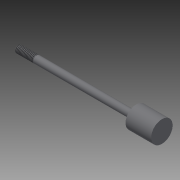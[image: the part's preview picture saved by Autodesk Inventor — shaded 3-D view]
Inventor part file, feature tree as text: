
AUTODESK INVENTOR PART (.ipt)
format: ipt  version: 2014 (Build 180170000, 170)  size: 131,072 bytes
history: native  units: in
note: dims shown in document units (in); Inventor stores cm internally (conversion verified against a paired STEP export)
features: other x49, revolve x3, sketch x3, thread x1
ambient origin geometry x8: Origin, YZ Plane, XZ Plane, XY Plane, X Axis, Y Axis, Z Axis, Center Point
bodies: Solid1 (feature_tree)
feature tree (56):
  revolve  "Revolution1"  [1 undecoded]
  thread  "Thread1"  [1 undecoded]
  revolve  "Revolution2"  [1 undecoded]
  revolve  "Revolution3"  [1 undecoded]
  other  "h1_XY"
  other  "h1_YZ"
  other  "h1_ZX"
  other  "h1_X"
  other  "h1_Y"
  other  "h1_Z"
  other  "h1_Center"
  other  "h2_XY"
  other  "h2_YZ"
  other  "h2_ZX"
  other  "h2_X"
  other  "h2_Y"
  other  "h2_Z"
  other  "h2_Center"
  other  "k1_XY"
  other  "k1_YZ"
  other  "k1_ZX"
  other  "k1_X"
  other  "k1_Y"
  other  "k1_Z"
  other  "k1_Center"
  other  "k2_XY"
  other  "k2_YZ"
  other  "k2_ZX"
  other  "k2_X"
  other  "k2_Y"
  other  "k2_Z"
  other  "k2_Center"
  other  "start_XY"
  other  "start_YZ"
  other  "start_ZX"
  other  "start_X"
  other  "start_Y"
  other  "start_Z"
  other  "start_Center"
  other  "to_prc_XY"
  other  "to_prc_YZ"
  other  "to_prc_ZX"
  other  "to_prc_X"
  other  "to_prc_Y"
  other  "to_prc_Z"
  other  "to_prc_Center"
  other  "to_rod_guide_XY"
  other  "to_rod_guide_YZ"
  other  "to_rod_guide_ZX"
  other  "to_rod_guide_X"
  other  "to_rod_guide_Y"
  other  "to_rod_guide_Z"
  other  "to_rod_guide_Center"
  sketch  "Sketch_3"  dims[d0=360.0deg d1=0.49in d2=3.291in d3=360.0deg]
  sketch  "Sketch_17"
  sketch  "Sketch_12"  dims[d4=360.0deg]
note: 4 required parameter values undecoded (feature->parameter linkage not recoverable at this tier; creation-order binding heuristic only, values carry confidence <= 0.55)